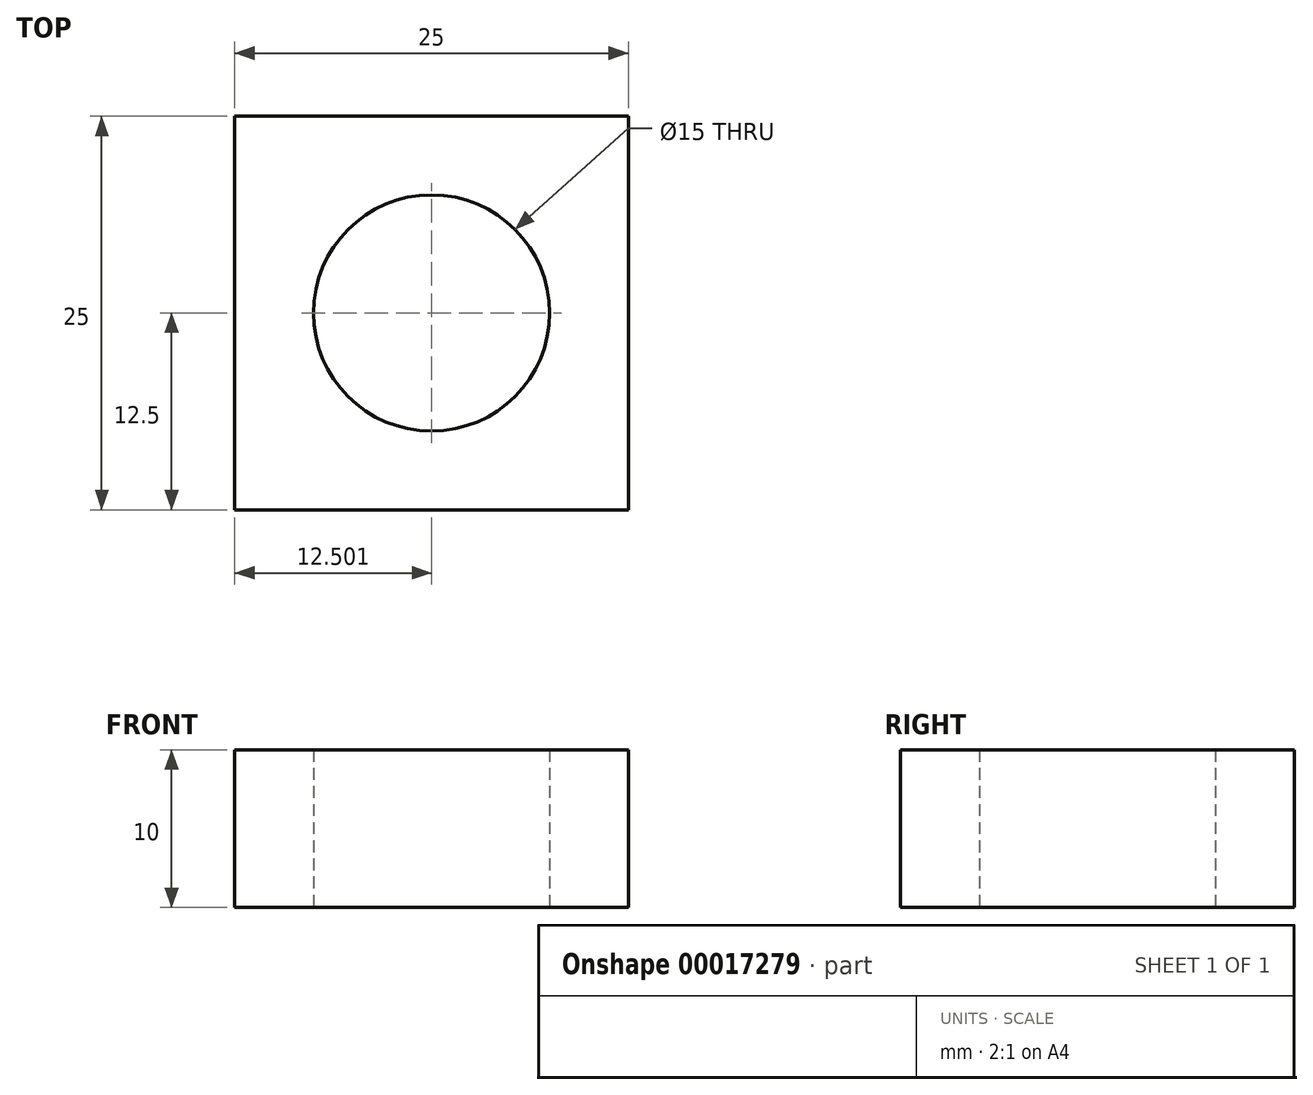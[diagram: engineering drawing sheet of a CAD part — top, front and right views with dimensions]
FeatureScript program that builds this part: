
annotation { "Feature Type Name" : "Feature", "Feature Type Description" : "" }
export const myFeature = defineFeature(function(context is Context, id is Id, definition is map)
    precondition{}
    {
        {
            var Q0;
            Q0=qCreatedBy(makeId("Top.planeOp"),FACE);
            var sketch = newSketch(context, id + "F0", { "sketchPlane" : qUnion([Q0])});
            skLineSegment(sketch, "E0.bottom", {"start": v(-19.92, 25) * mm, "end": v(5.08, 25) * mm});
            skLineSegment(sketch, "E0.top", {"start": v(-19.92, 0) * mm, "end": v(5.08, 0) * mm});
            skLineSegment(sketch, "E0.left", {"start": v(-19.92, 25) * mm, "end": v(-19.92, 0) * mm});
            skLineSegment(sketch, "E0.right", {"start": v(5.08, 25) * mm, "end": v(5.08, 0) * mm});
            skCircle(sketch, "E1", {"center": v(-7.42, 12.5) * mm, "radius": 7.5 * mm});
            skSolve(sketch);
        }
        {
            var Q0;
            Q0=makeQuery(id+"F0.imprint","IMPRINT",FACE,{"disambiguationData":[TD([[makeQuery(id+"F0.imprint","IMPRINT",EDGE,{"derivedFrom":sQuery(id+"F0.wireOp",EDGE,"E0.bottom")}),-1.0]])]});
            extrude(context, id + "F1", {"entities" : qUnion([Q0]), "depth" : 10 * mm});
        }
    });
